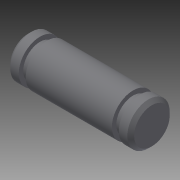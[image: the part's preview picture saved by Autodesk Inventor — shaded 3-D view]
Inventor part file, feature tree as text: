
AUTODESK INVENTOR PART (.ipt)
format: ipt  version: 2014 (Build 180170000, 170)  size: 125,440 bytes
history: native  units: in
note: dims shown in document units (in); Inventor stores cm internally (conversion verified against a paired STEP export)
features: other x49, revolve x1, sketch x1
ambient origin geometry x8: Origin, YZ Plane, XZ Plane, XY Plane, X Axis, Y Axis, Z Axis, Center Point
bodies: Solid1 (feature_tree)
feature tree (51):
  revolve  "Revolution1"  [1 undecoded]
  other  "p1_XY"
  other  "p1_YZ"
  other  "p1_ZX"
  other  "p1_X"
  other  "p1_Y"
  other  "p1_Z"
  other  "p1_Center"
  other  "p2_XY"
  other  "p2_YZ"
  other  "p2_ZX"
  other  "p2_X"
  other  "p2_Y"
  other  "p2_Z"
  other  "p2_Center"
  other  "pin_XY"
  other  "pin_YZ"
  other  "pin_ZX"
  other  "pin_X"
  other  "pin_Y"
  other  "pin_Z"
  other  "pin_Center"
  other  "rr1_XY"
  other  "rr1_YZ"
  other  "rr1_ZX"
  other  "rr1_X"
  other  "rr1_Y"
  other  "rr1_Z"
  other  "rr1_Center"
  other  "rr2_XY"
  other  "rr2_YZ"
  other  "rr2_ZX"
  other  "rr2_X"
  other  "rr2_Y"
  other  "rr2_Z"
  other  "rr2_Center"
  other  "w21_XY"
  other  "w21_YZ"
  other  "w21_ZX"
  other  "w21_X"
  other  "w21_Y"
  other  "w21_Z"
  other  "w21_Center"
  other  "w22_XY"
  other  "w22_YZ"
  other  "w22_ZX"
  other  "w22_X"
  other  "w22_Y"
  other  "w22_Z"
  other  "w22_Center"
  sketch  "Sketch_1"  dims[d0=360.0deg]
note: 1 required parameter value undecoded (feature->parameter linkage not recoverable at this tier; creation-order binding heuristic only, values carry confidence <= 0.55)
